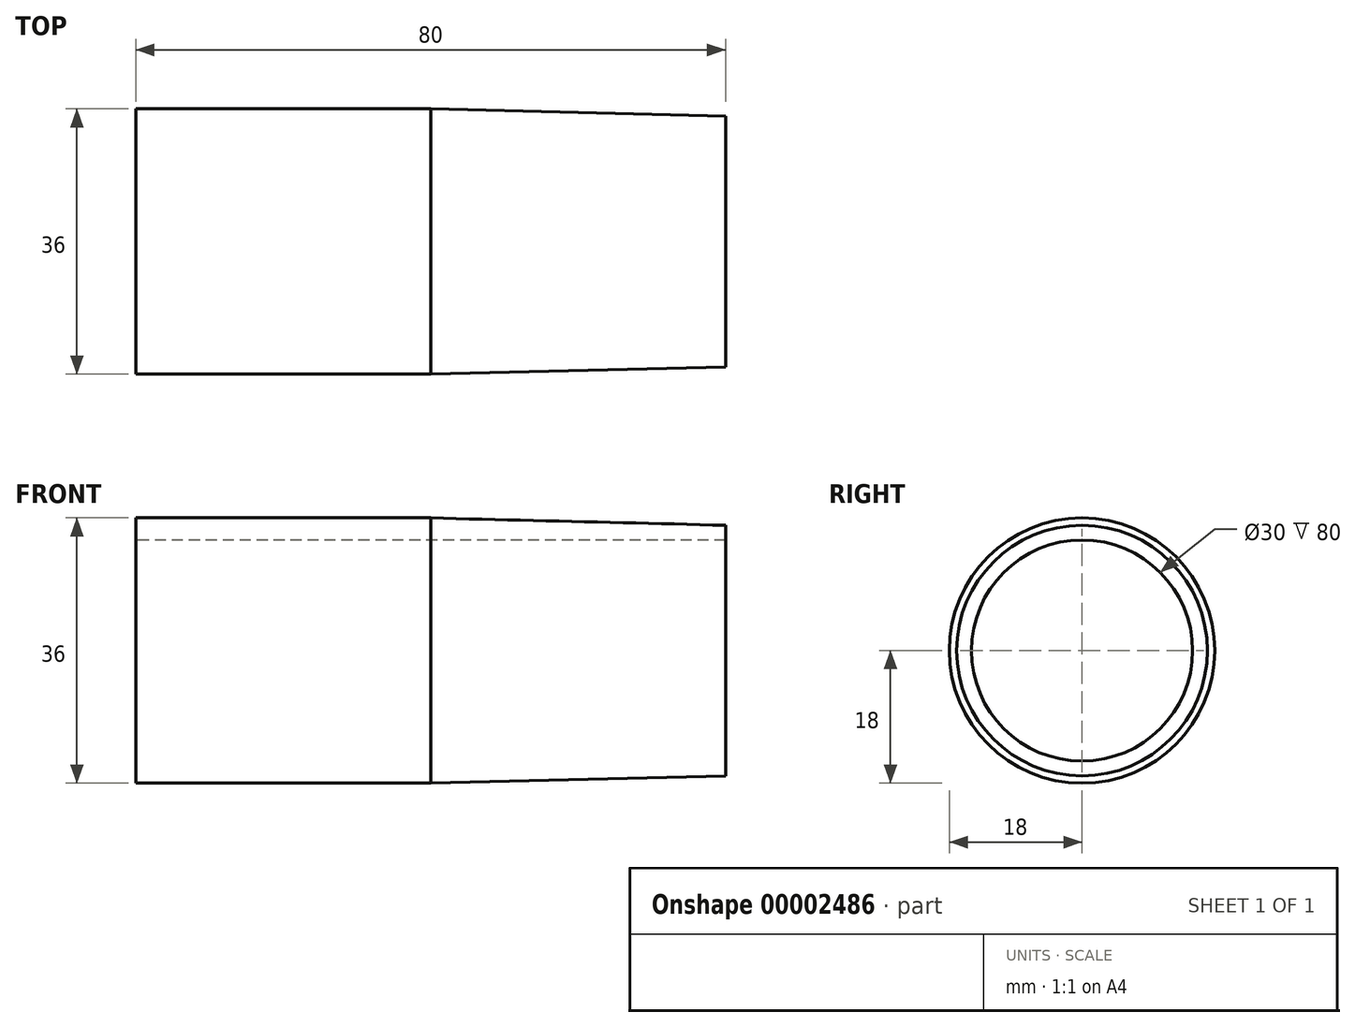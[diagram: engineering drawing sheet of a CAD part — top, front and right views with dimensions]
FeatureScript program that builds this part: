
annotation { "Feature Type Name" : "Feature", "Feature Type Description" : "" }
export const myFeature = defineFeature(function(context is Context, id is Id, definition is map)
    precondition{}
    {
        {
            var Q0;
            Q0=qCreatedBy(makeId("Front.planeOp"),FACE);
            var sketch = newSketch(context, id + "F0", { "sketchPlane" : qUnion([Q0])});
            skLineSegment(sketch, "E0", {"start": v(-45.87, 0) * mm, "end": v(46.06, 0) * mm, "construction": true});
            skLineSegment(sketch, "E1", {"start": v(-40, 15) * mm, "end": v(40, 15) * mm});
            skLineSegment(sketch, "E2", {"start": v(40, 15) * mm, "end": v(40, 17) * mm});
            skLineSegment(sketch, "E3", {"start": v(40, 17) * mm, "end": v(0, 18) * mm});
            skLineSegment(sketch, "E4", {"start": v(0, 18) * mm, "end": v(-40, 18) * mm});
            skLineSegment(sketch, "E5", {"start": v(-40, 18) * mm, "end": v(-40, 15) * mm});
            skSolve(sketch);
        }
        {
            var Q0;
            Q0=makeQuery(id+"F0.imprint","IMPRINT",FACE,{"disambiguationData":[TD([[makeQuery(id+"F0.imprint","IMPRINT",EDGE,{"derivedFrom":sQuery(id+"F0.wireOp",EDGE,"E1")}),1.0]])]});
            var Q1;
            Q1=sQuery(id+"F0.wireOp",EDGE,"E0");
            revolve(context, id + "F1", {"entities" : qUnion([Q0]), "axis" : qUnion([Q1]), "revolveType" : RevolveType.FULL});
        }
    });
